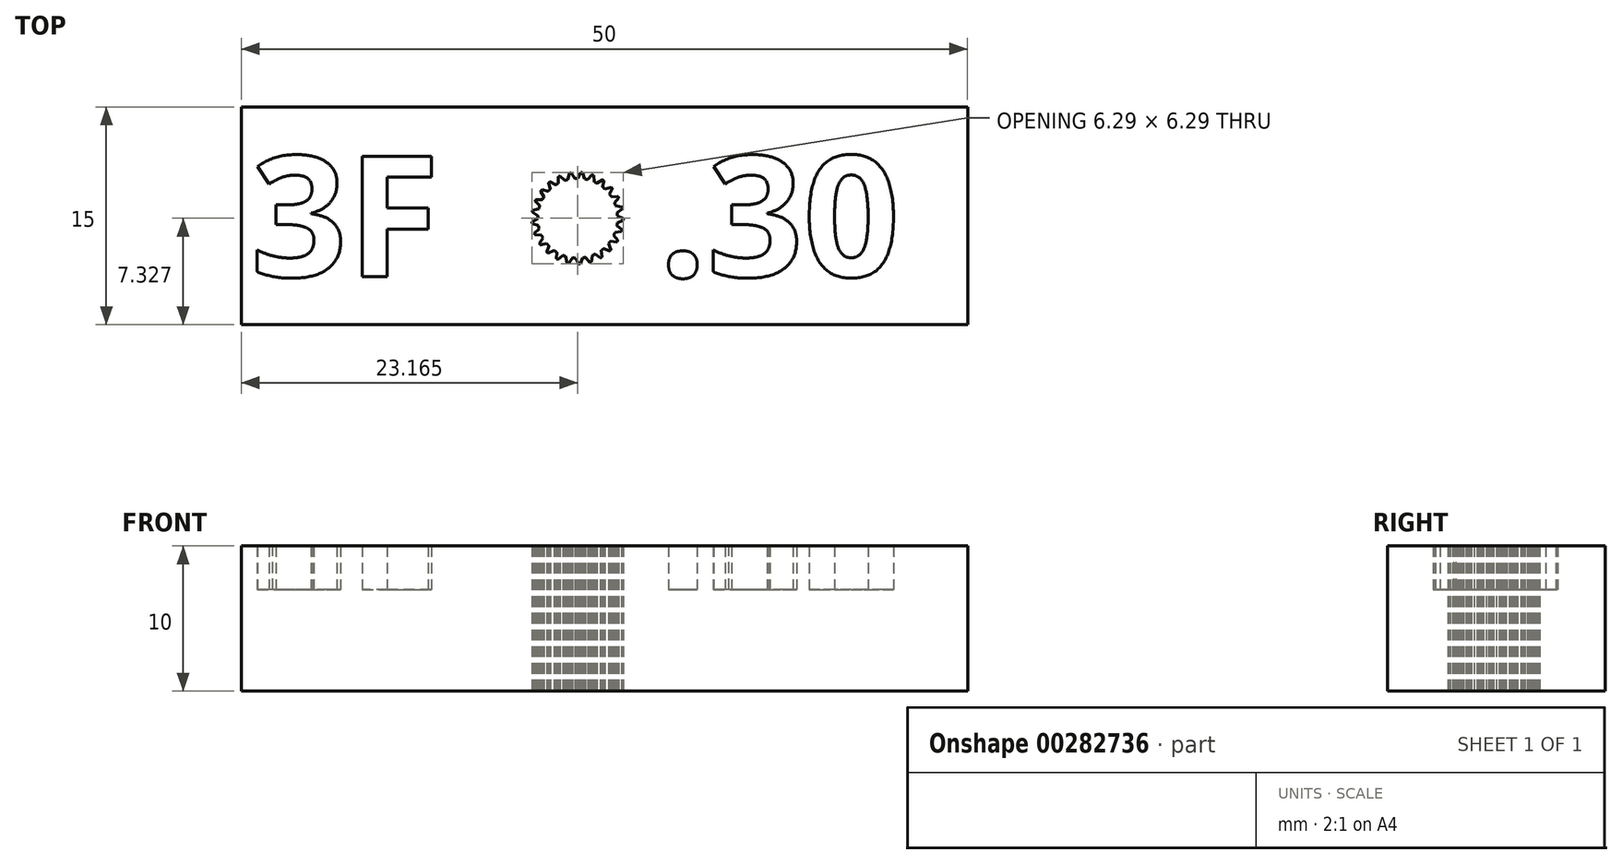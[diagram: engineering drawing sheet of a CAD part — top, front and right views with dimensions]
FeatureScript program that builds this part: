
annotation { "Feature Type Name" : "Feature", "Feature Type Description" : "" }
export const myFeature = defineFeature(function(context is Context, id is Id, definition is map)
    precondition{}
    {
        {
            var Q0;
            Q0=qCreatedBy(makeId("Top.planeOp"),FACE);
            var sketch = newSketch(context, id + "F0", { "sketchPlane" : qUnion([Q0])});
            skLineSegment(sketch, "E0.bottom", {"start": v(26.84, -7.33) * mm, "end": v(-23.16, -7.33) * mm});
            skLineSegment(sketch, "E0.top", {"start": v(26.84, 7.67) * mm, "end": v(-23.16, 7.67) * mm});
            skLineSegment(sketch, "E0.left", {"start": v(26.84, -7.33) * mm, "end": v(26.84, 7.67) * mm});
            skLineSegment(sketch, "E0.right", {"start": v(-23.16, -7.33) * mm, "end": v(-23.16, 7.67) * mm});
            skText(sketch, "E1", { "text": "3F     .30", "fontName": "OpenSans-Bold.ttf"});
            skLineSegment(sketch, "E2", {"start": v(10, 7.67) * mm, "end": v(10, 4.35) * mm, "construction": true});
            skLineSegment(sketch, "E3", {"start": v(8.84, -4.02) * mm, "end": v(8.84, -7.33) * mm, "construction": true});
            skCircle(sketch, "E4", {"center": v(0, 0) * mm, "radius": 2.75 * mm, "construction": true});
            skArc(sketch, "E5", {"start": v(0.21, 3.14) * mm, "mid": v(-0.28, -3.14) * mm, "end": v(0.34, 3.13) * mm, "construction": true});
            skLineSegment(sketch, "E6", {"start": v(0, 0) * mm, "end": v(0.82, 3.2) * mm, "construction": true});
            skLineSegment(sketch, "E7", {"start": v(0, 0) * mm, "end": v(0.58, 3.25) * mm, "construction": true});
            skLineSegment(sketch, "E8", {"start": v(0, 0) * mm, "end": v(0.21, 3.16) * mm, "construction": true});
            skLineSegment(sketch, "E9", {"start": v(0, 0) * mm, "end": v(0.36, 3.28) * mm, "construction": true});
            skLineSegment(sketch, "E10", {"start": v(0, 2.75) * mm, "end": v(0.21, 3.14) * mm});
            skLineSegment(sketch, "E11", {"start": v(0.34, 3.13) * mm, "end": v(0.48, 2.7) * mm});
            skArc(sketch, "E12", {"start": v(0.21, 3.14) * mm, "mid": v(0.28, 3.14) * mm, "end": v(0.34, 3.13) * mm});
            skArc(sketch, "E13", {"start": v(0.48, 2.7) * mm, "mid": v(0.58, 2.69) * mm, "end": v(0.68, 2.66) * mm});
            skLineSegment(sketch, "E14.1.0", {"start": v(-0.68, 2.66) * mm, "end": v(-0.58, 3.1) * mm});
            skArc(sketch, "E14.1.1", {"start": v(-0.58, 3.1) * mm, "mid": v(-0.51, 3.1) * mm, "end": v(-0.45, 3.12) * mm});
            skLineSegment(sketch, "E14.1.2", {"start": v(-0.45, 3.12) * mm, "end": v(-0.2, 2.74) * mm});
            skArc(sketch, "E14.1.3", {"start": v(-0.2, 2.74) * mm, "mid": v(-0.1, 2.75) * mm, "end": v(0, 2.75) * mm});
            skLineSegment(sketch, "E14.2.0", {"start": v(-1.32, 2.4) * mm, "end": v(-1.33, 2.86) * mm});
            skArc(sketch, "E14.2.1", {"start": v(-1.33, 2.86) * mm, "mid": v(-1.27, 2.88) * mm, "end": v(-1.2, 2.9) * mm});
            skLineSegment(sketch, "E14.2.2", {"start": v(-1.21, 2.91) * mm, "end": v(-0.88, 2.6) * mm});
            skArc(sketch, "E14.2.3", {"start": v(-0.88, 2.6) * mm, "mid": v(-0.78, 2.64) * mm, "end": v(-0.68, 2.66) * mm});
            skLineSegment(sketch, "E14.3.0", {"start": v(-1.88, 2) * mm, "end": v(-2, 2.44) * mm});
            skArc(sketch, "E14.3.1", {"start": v(-2, 2.44) * mm, "mid": v(-1.95, 2.48) * mm, "end": v(-1.9, 2.52) * mm});
            skLineSegment(sketch, "E14.3.2", {"start": v(-1.9, 2.52) * mm, "end": v(-1.5, 2.3) * mm});
            skArc(sketch, "E14.3.3", {"start": v(-1.5, 2.3) * mm, "mid": v(-1.42, 2.36) * mm, "end": v(-1.32, 2.4) * mm});
            skLineSegment(sketch, "E14.4.0", {"start": v(-2.32, 1.47) * mm, "end": v(-2.54, 1.86) * mm});
            skArc(sketch, "E14.4.1", {"start": v(-2.54, 1.86) * mm, "mid": v(-2.5, 1.91) * mm, "end": v(-2.46, 1.97) * mm});
            skLineSegment(sketch, "E14.4.2", {"start": v(-2.46, 1.97) * mm, "end": v(-2.03, 1.86) * mm});
            skArc(sketch, "E14.4.3", {"start": v(-2.03, 1.86) * mm, "mid": v(-1.96, 1.93) * mm, "end": v(-1.88, 2) * mm});
            skLineSegment(sketch, "E14.5.0", {"start": v(-2.62, 0.85) * mm, "end": v(-2.92, 1.17) * mm});
            skArc(sketch, "E14.5.1", {"start": v(-2.92, 1.17) * mm, "mid": v(-2.9, 1.23) * mm, "end": v(-2.87, 1.3) * mm});
            skLineSegment(sketch, "E14.5.2", {"start": v(-2.88, 1.3) * mm, "end": v(-2.43, 1.3) * mm});
            skArc(sketch, "E14.5.3", {"start": v(-2.43, 1.3) * mm, "mid": v(-2.38, 1.38) * mm, "end": v(-2.32, 1.47) * mm});
            skLineSegment(sketch, "E14.6.0", {"start": v(-2.74, 0.17) * mm, "end": v(-3.12, 0.4) * mm});
            skArc(sketch, "E14.6.1", {"start": v(-3.12, 0.4) * mm, "mid": v(-3.11, 0.47) * mm, "end": v(-3.1, 0.54) * mm});
            skLineSegment(sketch, "E14.6.2", {"start": v(-3.1, 0.54) * mm, "end": v(-2.67, 0.65) * mm});
            skArc(sketch, "E14.6.3", {"start": v(-2.67, 0.65) * mm, "mid": v(-2.65, 0.75) * mm, "end": v(-2.62, 0.85) * mm});
            skLineSegment(sketch, "E14.7.0", {"start": v(-2.7, -0.52) * mm, "end": v(-3.13, -0.38) * mm});
            skArc(sketch, "E14.7.1", {"start": v(-3.13, -0.38) * mm, "mid": v(-3.13, -0.32) * mm, "end": v(-3.14, -0.25) * mm});
            skLineSegment(sketch, "E14.7.2", {"start": v(-3.14, -0.25) * mm, "end": v(-2.75, -0.04) * mm});
            skArc(sketch, "E14.7.3", {"start": v(-2.75, -0.04) * mm, "mid": v(-2.75, 0.07) * mm, "end": v(-2.74, 0.17) * mm});
            skLineSegment(sketch, "E14.8.0", {"start": v(-2.49, -1.17) * mm, "end": v(-2.93, -1.15) * mm});
            skArc(sketch, "E14.8.1", {"start": v(-2.93, -1.15) * mm, "mid": v(-2.96, -1.09) * mm, "end": v(-2.98, -1.02) * mm});
            skLineSegment(sketch, "E14.8.2", {"start": v(-2.98, -1.03) * mm, "end": v(-2.65, -0.72) * mm});
            skArc(sketch, "E14.8.3", {"start": v(-2.65, -0.72) * mm, "mid": v(-2.68, -0.62) * mm, "end": v(-2.7, -0.52) * mm});
            skLineSegment(sketch, "E14.9.0", {"start": v(-2.12, -1.75) * mm, "end": v(-2.56, -1.84) * mm});
            skArc(sketch, "E14.9.1", {"start": v(-2.56, -1.84) * mm, "mid": v(-2.6, -1.79) * mm, "end": v(-2.63, -1.73) * mm});
            skLineSegment(sketch, "E14.9.2", {"start": v(-2.63, -1.74) * mm, "end": v(-2.4, -1.36) * mm});
            skArc(sketch, "E14.9.3", {"start": v(-2.4, -1.36) * mm, "mid": v(-2.44, -1.26) * mm, "end": v(-2.49, -1.17) * mm});
            skLineSegment(sketch, "E14.10.0", {"start": v(-1.62, -2.22) * mm, "end": v(-2.02, -2.42) * mm});
            skArc(sketch, "E14.10.1", {"start": v(-2.02, -2.42) * mm, "mid": v(-2.07, -2.38) * mm, "end": v(-2.12, -2.33) * mm});
            skLineSegment(sketch, "E14.10.2", {"start": v(-2.12, -2.34) * mm, "end": v(-1.98, -1.9) * mm});
            skArc(sketch, "E14.10.3", {"start": v(-1.98, -1.9) * mm, "mid": v(-2.05, -1.83) * mm, "end": v(-2.12, -1.75) * mm});
            skLineSegment(sketch, "E14.11.0", {"start": v(-1.01, -2.56) * mm, "end": v(-1.35, -2.84) * mm});
            skArc(sketch, "E14.11.1", {"start": v(-1.35, -2.84) * mm, "mid": v(-1.41, -2.82) * mm, "end": v(-1.47, -2.79) * mm});
            skLineSegment(sketch, "E14.11.2", {"start": v(-1.47, -2.79) * mm, "end": v(-1.44, -2.34) * mm});
            skArc(sketch, "E14.11.3", {"start": v(-1.44, -2.34) * mm, "mid": v(-1.53, -2.28) * mm, "end": v(-1.62, -2.22) * mm});
            skLineSegment(sketch, "E14.12.0", {"start": v(-0.34, -2.73) * mm, "end": v(-0.6, -3.1) * mm});
            skArc(sketch, "E14.12.1", {"start": v(-0.6, -3.1) * mm, "mid": v(-0.67, -3.08) * mm, "end": v(-0.73, -3.06) * mm});
            skLineSegment(sketch, "E14.12.2", {"start": v(-0.73, -3.07) * mm, "end": v(-0.82, -2.63) * mm});
            skArc(sketch, "E14.12.3", {"start": v(-0.82, -2.63) * mm, "mid": v(-0.91, -2.6) * mm, "end": v(-1.01, -2.56) * mm});
            skLineSegment(sketch, "E14.13.0", {"start": v(0.34, -2.73) * mm, "end": v(0.18, -3.14) * mm});
            skArc(sketch, "E14.13.1", {"start": v(0.18, -3.14) * mm, "mid": v(0.12, -3.15) * mm, "end": v(0.05, -3.15) * mm});
            skLineSegment(sketch, "E14.13.2", {"start": v(0.06, -3.15) * mm, "end": v(-0.14, -2.75) * mm});
            skArc(sketch, "E14.13.3", {"start": v(-0.14, -2.75) * mm, "mid": v(-0.24, -2.74) * mm, "end": v(-0.34, -2.73) * mm});
            skLineSegment(sketch, "E14.14.0", {"start": v(1.01, -2.56) * mm, "end": v(0.96, -3) * mm});
            skArc(sketch, "E14.14.1", {"start": v(0.96, -3) * mm, "mid": v(0.9, -3.02) * mm, "end": v(0.84, -3.04) * mm});
            skLineSegment(sketch, "E14.14.2", {"start": v(0.84, -3.04) * mm, "end": v(0.55, -2.7) * mm});
            skArc(sketch, "E14.14.3", {"start": v(0.55, -2.7) * mm, "mid": v(0.45, -2.71) * mm, "end": v(0.34, -2.73) * mm});
            skLineSegment(sketch, "E14.15.0", {"start": v(1.62, -2.22) * mm, "end": v(1.68, -2.67) * mm});
            skArc(sketch, "E14.15.1", {"start": v(1.68, -2.67) * mm, "mid": v(1.62, -2.7) * mm, "end": v(1.56, -2.73) * mm});
            skLineSegment(sketch, "E14.15.2", {"start": v(1.57, -2.74) * mm, "end": v(1.2, -2.47) * mm});
            skArc(sketch, "E14.15.3", {"start": v(1.2, -2.47) * mm, "mid": v(1.1, -2.52) * mm, "end": v(1.01, -2.56) * mm});
            skLineSegment(sketch, "E14.16.0", {"start": v(2.12, -1.75) * mm, "end": v(2.29, -2.17) * mm});
            skArc(sketch, "E14.16.1", {"start": v(2.29, -2.17) * mm, "mid": v(2.24, -2.21) * mm, "end": v(2.2, -2.26) * mm});
            skLineSegment(sketch, "E14.16.2", {"start": v(2.2, -2.26) * mm, "end": v(1.78, -2.1) * mm});
            skArc(sketch, "E14.16.3", {"start": v(1.78, -2.1) * mm, "mid": v(1.7, -2.16) * mm, "end": v(1.62, -2.22) * mm});
            skLineSegment(sketch, "E14.17.0", {"start": v(2.49, -1.17) * mm, "end": v(2.75, -1.53) * mm});
            skArc(sketch, "E14.17.1", {"start": v(2.75, -1.53) * mm, "mid": v(2.72, -1.59) * mm, "end": v(2.69, -1.64) * mm});
            skLineSegment(sketch, "E14.17.2", {"start": v(2.7, -1.64) * mm, "end": v(2.25, -1.59) * mm});
            skArc(sketch, "E14.17.3", {"start": v(2.25, -1.59) * mm, "mid": v(2.18, -1.67) * mm, "end": v(2.12, -1.75) * mm});
            skLineSegment(sketch, "E14.18.0", {"start": v(2.7, -0.52) * mm, "end": v(3.05, -0.8) * mm});
            skArc(sketch, "E14.18.1", {"start": v(3.05, -0.8) * mm, "mid": v(3.03, -0.86) * mm, "end": v(3.01, -0.92) * mm});
            skLineSegment(sketch, "E14.18.2", {"start": v(3.01, -0.92) * mm, "end": v(2.57, -0.98) * mm});
            skArc(sketch, "E14.18.3", {"start": v(2.57, -0.98) * mm, "mid": v(2.53, -1.08) * mm, "end": v(2.49, -1.17) * mm});
            skLineSegment(sketch, "E14.19.0", {"start": v(2.74, 0.17) * mm, "end": v(3.15, -0.01) * mm});
            skArc(sketch, "E14.19.1", {"start": v(3.15, -0.01) * mm, "mid": v(3.15, -0.08) * mm, "end": v(3.15, -0.14) * mm});
            skLineSegment(sketch, "E14.19.2", {"start": v(3.15, -0.14) * mm, "end": v(2.73, -0.3) * mm});
            skArc(sketch, "E14.19.3", {"start": v(2.73, -0.3) * mm, "mid": v(2.72, -0.41) * mm, "end": v(2.7, -0.52) * mm});
            skLineSegment(sketch, "E14.20.0", {"start": v(2.62, 0.85) * mm, "end": v(3.05, 0.77) * mm});
            skArc(sketch, "E14.20.1", {"start": v(3.05, 0.77) * mm, "mid": v(3.07, 0.7) * mm, "end": v(3.08, 0.64) * mm});
            skLineSegment(sketch, "E14.20.2", {"start": v(3.09, 0.64) * mm, "end": v(2.72, 0.38) * mm});
            skArc(sketch, "E14.20.3", {"start": v(2.72, 0.38) * mm, "mid": v(2.74, 0.28) * mm, "end": v(2.74, 0.17) * mm});
            skLineSegment(sketch, "E14.21.0", {"start": v(2.32, 1.47) * mm, "end": v(2.77, 1.5) * mm});
            skArc(sketch, "E14.21.1", {"start": v(2.77, 1.5) * mm, "mid": v(2.8, 1.45) * mm, "end": v(2.83, 1.4) * mm});
            skLineSegment(sketch, "E14.21.2", {"start": v(2.83, 1.4) * mm, "end": v(2.54, 1.05) * mm});
            skArc(sketch, "E14.21.3", {"start": v(2.54, 1.05) * mm, "mid": v(2.58, 0.95) * mm, "end": v(2.62, 0.85) * mm});
            skLineSegment(sketch, "E14.22.0", {"start": v(1.88, 2) * mm, "end": v(2.3, 2.15) * mm});
            skArc(sketch, "E14.22.1", {"start": v(2.3, 2.15) * mm, "mid": v(2.35, 2.1) * mm, "end": v(2.4, 2.05) * mm});
            skLineSegment(sketch, "E14.22.2", {"start": v(2.4, 2.05) * mm, "end": v(2.2, 1.65) * mm});
            skArc(sketch, "E14.22.3", {"start": v(2.2, 1.65) * mm, "mid": v(2.26, 1.56) * mm, "end": v(2.32, 1.47) * mm});
            skLineSegment(sketch, "E14.23.0", {"start": v(1.32, 2.4) * mm, "end": v(1.7, 2.65) * mm});
            skArc(sketch, "E14.23.1", {"start": v(1.7, 2.65) * mm, "mid": v(1.75, 2.62) * mm, "end": v(1.8, 2.58) * mm});
            skLineSegment(sketch, "E14.23.2", {"start": v(1.8, 2.58) * mm, "end": v(1.73, 2.14) * mm});
            skArc(sketch, "E14.23.3", {"start": v(1.73, 2.14) * mm, "mid": v(1.8, 2.07) * mm, "end": v(1.88, 2) * mm});
            skLineSegment(sketch, "E14.24.0", {"start": v(0.68, 2.66) * mm, "end": v(0.99, 3) * mm});
            skArc(sketch, "E14.24.1", {"start": v(0.99, 3) * mm, "mid": v(1.05, 2.97) * mm, "end": v(1.1, 2.95) * mm});
            skLineSegment(sketch, "E14.24.2", {"start": v(1.1, 2.95) * mm, "end": v(1.14, 2.5) * mm});
            skArc(sketch, "E14.24.3", {"start": v(1.14, 2.5) * mm, "mid": v(1.23, 2.46) * mm, "end": v(1.32, 2.4) * mm});
            const initialGuessF0  = {"E1": [-0.0225, -0.00402, 1, 0, 0.00836]};
            skSetInitialGuess(sketch, initialGuessF0);
            skSolve(sketch);
        }
        {
            var Q0;
            {var subQ133=sQuery(id+"F0.wireOp",EDGE,"cx5UNcc4-gtU0-2td0-y6or-8MBt4QoFyyIK");Q0=makeQuery(id+"F0.imprint","IMPRINT",FACE,{"disambiguationData":[TD([[makeQuery(id+"F0.imprint","IMPRINT",EDGE,{"derivedFrom":subQ133}),1.0]])]});}
            var Q1;
            Q1=makeQuery(id+"F0.imprint","IMPRINT",FACE,{"disambiguationData":[TD([[makeQuery(id+"F0.imprint","IMPRINT",EDGE,{"derivedFrom":sQuery(id+"F0.wireOp",EDGE,"E1.sketch_text.stroke-89")}),1.0]])]});
            var Q2;
            Q2=makeQuery(id+"F0.imprint","IMPRINT",FACE,{"disambiguationData":[TD([[makeQuery(id+"F0.imprint","IMPRINT",EDGE,{"derivedFrom":sQuery(id+"F0.wireOp",EDGE,"E1.sketch_text.stroke-78")}),1.0]])]});
            var Q3;
            Q3=makeQuery(id+"F0.imprint","IMPRINT",FACE,{"disambiguationData":[TD([[makeQuery(id+"F0.imprint","IMPRINT",EDGE,{"derivedFrom":sQuery(id+"F0.wireOp",EDGE,"E0.bottom")}),-1.0]])]});
            var Q4;
            Q4=makeQuery(id+"F0.imprint","IMPRINT",FACE,{"disambiguationData":[TD([[makeQuery(id+"F0.imprint","IMPRINT",EDGE,{"derivedFrom":sQuery(id+"F0.wireOp",EDGE,"E1.sketch_text.stroke-80")}),1.0]])]});
            extrude(context, id + "F1", {"entities" : qUnion([Q0, Q1, Q2, Q3, Q4]), "depth" : 10 * mm});
        }
        {
            var Q0;
            Q0=makeQuery(id+"F0.imprint","IMPRINT",FACE,{"disambiguationData":[TD([[makeQuery(id+"F0.imprint","IMPRINT",EDGE,{"derivedFrom":sQuery(id+"F0.wireOp",EDGE,"E1.sketch_text.stroke-0")}),-1.0]])]});
            var Q1;
            Q1=makeQuery(id+"F0.imprint","IMPRINT",FACE,{"disambiguationData":[TD([[makeQuery(id+"F0.imprint","IMPRINT",EDGE,{"derivedFrom":sQuery(id+"F0.wireOp",EDGE,"E1.sketch_text.stroke-24")}),-1.0]])]});
            var Q2;
            Q2=makeQuery(id+"F0.imprint","IMPRINT",FACE,{"disambiguationData":[TD([[makeQuery(id+"F0.imprint","IMPRINT",EDGE,{"derivedFrom":sQuery(id+"F0.wireOp",EDGE,"E1.sketch_text.stroke-49")}),-1.0]])]});
            var Q3;
            Q3=makeQuery(id+"F0.imprint","IMPRINT",FACE,{"disambiguationData":[TD([[makeQuery(id+"F0.imprint","IMPRINT",EDGE,{"derivedFrom":sQuery(id+"F0.wireOp",EDGE,"E1.sketch_text.stroke-57")}),-1.0]])]});
            var Q4;
            Q4=makeQuery(id+"F0.imprint","IMPRINT",FACE,{"disambiguationData":[TD([[makeQuery(id+"F0.imprint","IMPRINT",EDGE,{"derivedFrom":sQuery(id+"F0.wireOp",EDGE,"E1.sketch_text.stroke-65")}),-1.0]])]});
            var Q5;
            Q5=makeQuery(id+"F0.imprint","IMPRINT",FACE,{"disambiguationData":[TD([[makeQuery(id+"F0.imprint","IMPRINT",EDGE,{"derivedFrom":sQuery(id+"F0.wireOp",EDGE,"E1.sketch_text.stroke-81")}),-1.0]])]});
            var Q6;
            Q6=makeQuery(id+"F0.imprint","IMPRINT",FACE,{"disambiguationData":[TD([[makeQuery(id+"F0.imprint","IMPRINT",EDGE,{"derivedFrom":sQuery(id+"F0.wireOp",EDGE,"E1.sketch_text.stroke-27")}),-1.0]])]});
            var Q7;
            Q7=makeQuery(id+"F0.imprint","IMPRINT",FACE,{"disambiguationData":[TD([[makeQuery(id+"F0.imprint","IMPRINT",EDGE,{"derivedFrom":sQuery(id+"F0.wireOp",EDGE,"E1.sketch_text.stroke-37")}),-1.0]])]});
            extrude(context, id + "F2", {"entities" : qUnion([Q0, Q1, Q2, Q3, Q4, Q5, Q6, Q7]), "operationType" : NewBodyOperationType.ADD, "depth" : 7 * mm});
        }
    });
